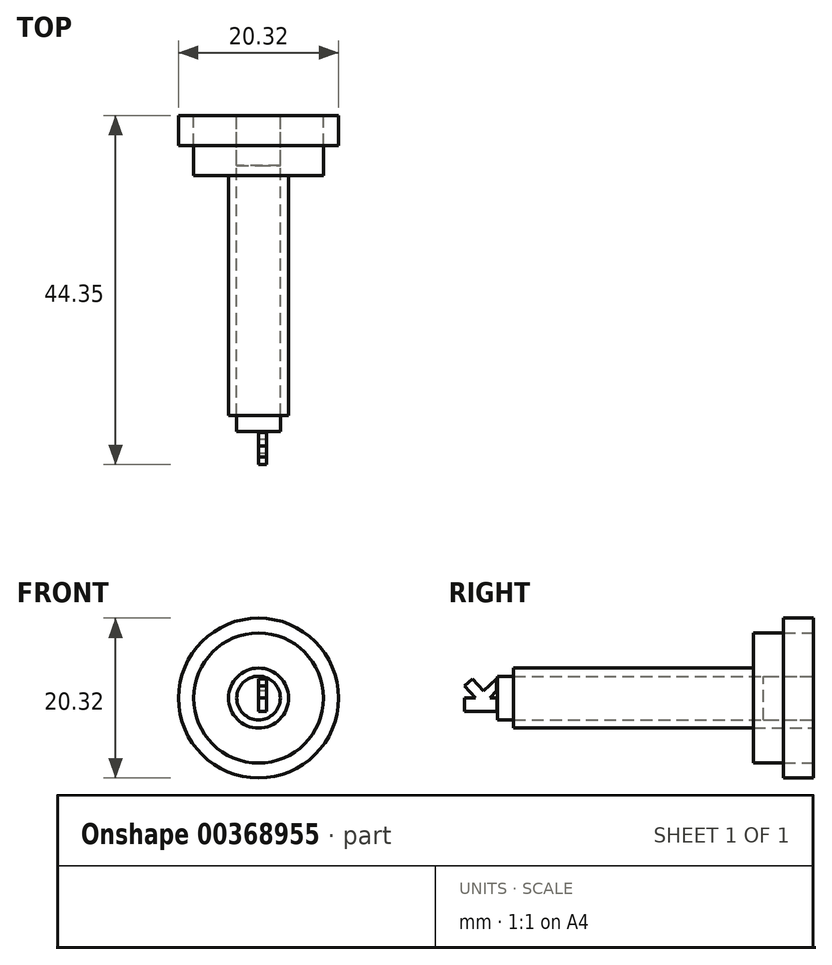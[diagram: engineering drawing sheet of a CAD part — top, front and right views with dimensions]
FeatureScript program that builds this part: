
annotation { "Feature Type Name" : "Feature", "Feature Type Description" : "" }
export const myFeature = defineFeature(function(context is Context, id is Id, definition is map)
    precondition{}
    {
        {
            var Q0;
            Q0=qCreatedBy(makeId("Front.planeOp"),FACE);
            var sketch = newSketch(context, id + "F0", { "sketchPlane" : qUnion([Q0])});
            skCircle(sketch, "E0", {"center": v(0, 0) * mm, "radius": 10.16 * mm});
            skSolve(sketch);
        }
        {
            var Q0;
            Q0 = qSketchRegion(id + "F0", true);
            extrude(context, id + "F1", {"entities" : qUnion([Q0]), "depth" : 3.8 * mm});
        }
        {
            var Q0;
            Q0=qCreatedBy(makeId("Front.planeOp"),FACE);
            var sketch = newSketch(context, id + "F2", { "sketchPlane" : qUnion([Q0])});
            skCircle(sketch, "E1", {"center": v(0, 0) * mm, "radius": 8.26 * mm});
            skSolve(sketch);
        }
        {
            var Q0;
            Q0=makeQuery(id+"F2.imprint","IMPRINT",FACE,{"disambiguationData":[TD([[makeQuery(id+"F2.imprint","IMPRINT",EDGE,{"derivedFrom":sQuery(id+"F2.wireOp",EDGE,"E1")}),1.0]])]});
            var Q1;
            Q1=sQuery(id+"F2.wireOp",EDGE,"E1");
            extrude(context, id + "F3", {"entities" : qUnion([Q0]), "surfaceEntities" : qUnion([Q1]), "depth" : 7.62 * mm});
        }
        {
            var Q0;
            Q0=qCreatedBy(makeId("Front.planeOp"),FACE);
            var sketch = newSketch(context, id + "F4", { "sketchPlane" : qUnion([Q0])});
            skCircle(sketch, "E2", {"center": v(0, 0) * mm, "radius": 3.81 * mm});
            skSolve(sketch);
        }
        {
            var Q0;
            Q0 = qSketchRegion(id + "F4", true);
            var Q1;
            Q1 = qSketchRegion(id + "F6", true);
            extrude(context, id + "F5", {"entities" : qUnion([Q0, Q1]), "depth" : 38.1 * mm});
        }
        {
            var Q0;
            Q0=qCreatedBy(makeId("Front.planeOp"),FACE);
            var sketch = newSketch(context, id + "F6", { "sketchPlane" : qUnion([Q0])});
            skCircle(sketch, "E3", {"center": v(0, 0) * mm, "radius": 2.77 * mm});
            skSolve(sketch);
        }
        {
            var Q0;
            Q0 = qSketchRegion(id + "F6", true);
            extrude(context, id + "F7", {"entities" : qUnion([Q0]), "depth" : 6.35 * mm});
        }
        {
            var Q0;
            Q0 = qSketchRegion(id + "F6", true);
            extrude(context, id + "F8", {"entities" : qUnion([Q0]), "depth" : 40.13 * mm});
        }
        {
            var Q0;
            Q0=qCreatedBy(makeId("Right.planeOp"),FACE);
            var sketch = newSketch(context, id + "F9", { "sketchPlane" : qUnion([Q0])});
            skLineSegment(sketch, "E4", {"start": v(-38.15, 0) * mm, "end": v(-17.97, 0) * mm, "construction": true});
            skLineSegment(sketch, "E5", {"start": v(-38.15, 0) * mm, "end": v(-38.15, 6.54) * mm});
            skLineSegment(sketch, "E6", {"start": v(-38.15, 6.54) * mm, "end": v(-17.97, 0) * mm});
            skSolve(sketch);
        }
        {
            var Q0;
            Q0=sQuery(id+"F9.wireOp",EDGE,"E5");
            var Q1;
            Q1=sQuery(id+"F9.wireOp",EDGE,"E6");
            var Q2;
            Q2=sQuery(id+"F9.wireOp",EDGE,"E4");
            revolve(context, id + "F10", {"bodyType" : ToolBodyType.SURFACE, "surfaceEntities" : qUnion([Q0, Q1]), "axis" : qUnion([Q2]), "revolveType" : RevolveType.FULL});
        }
        {
            var Q0;
            Q0=qCreatedBy(makeId("Right.planeOp"),FACE);
            var sketch = newSketch(context, id + "F11", { "sketchPlane" : qUnion([Q0])});
            skLineSegment(sketch, "E7", {"start": v(-40.2, 0) * mm, "end": v(-40.2, -1.67) * mm});
            skLineSegment(sketch, "E8", {"start": v(-40.2, -1.67) * mm, "end": v(-44.35, -1.67) * mm});
            skLineSegment(sketch, "E9", {"start": v(-44.35, -1.67) * mm, "end": v(-44.35, 0) * mm});
            skLineSegment(sketch, "E10", {"start": v(-44.35, 0) * mm, "end": v(-42.96, 0) * mm});
            skLineSegment(sketch, "E11", {"start": v(-42.96, 0) * mm, "end": v(-44.35, 1.51) * mm});
            skLineSegment(sketch, "E12", {"start": v(-44.35, 1.51) * mm, "end": v(-43.36, 2.42) * mm});
            skLineSegment(sketch, "E13", {"start": v(-43.36, 2.42) * mm, "end": v(-41.96, 0.9) * mm});
            skLineSegment(sketch, "E14", {"start": v(-41.96, 0.9) * mm, "end": v(-40.3, 2.42) * mm});
            skLineSegment(sketch, "E15", {"start": v(-40.2, 0) * mm, "end": v(-41.13, 0) * mm});
            skPoint(sketch, "E15.endSnap0", {"position": v(-41.13, 1.66) * mm});
            skLineSegment(sketch, "E16", {"start": v(-41.13, 0) * mm, "end": v(-40.3, 0.9) * mm});
            skLineSegment(sketch, "E17", {"start": v(-40.3, 2.42) * mm, "end": v(-40.3, 0.9) * mm});
            skSolve(sketch);
        }
        {
            var Q0;
            Q0 = qSketchRegion(id + "F11", true);
            extrude(context, id + "F12", {"entities" : qUnion([Q0]), "depth" : 1.02 * mm});
        }
    });
